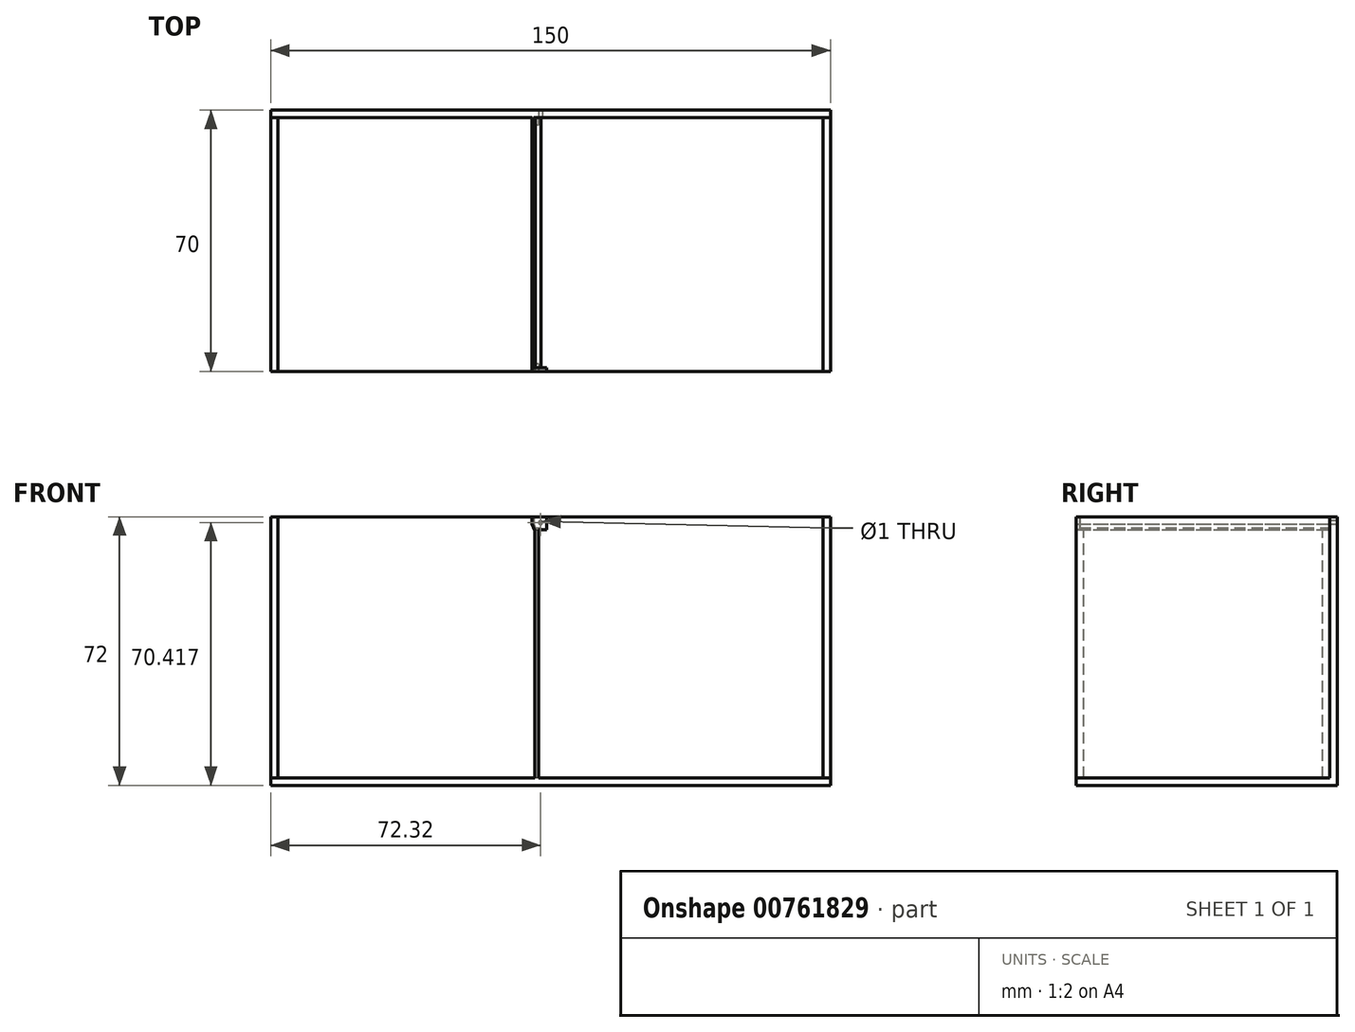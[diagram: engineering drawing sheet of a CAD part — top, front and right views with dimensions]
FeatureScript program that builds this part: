
annotation { "Feature Type Name" : "Feature", "Feature Type Description" : "" }
export const myFeature = defineFeature(function(context is Context, id is Id, definition is map)
    precondition{}
    {
        {
            var Q0;
            Q0=qCreatedBy(makeId("Front.planeOp"),FACE);
            var sketch = newSketch(context, id + "F0", { "sketchPlane" : qUnion([Q0])});
            skLineSegment(sketch, "E0.bottom", {"start": v(75, 35) * mm, "end": v(-75, 35) * mm});
            skLineSegment(sketch, "E0.top", {"start": v(75, -35) * mm, "end": v(-75, -35) * mm});
            skLineSegment(sketch, "E0.left", {"start": v(75, 35) * mm, "end": v(75, -35) * mm});
            skLineSegment(sketch, "E0.right", {"start": v(-75, 35) * mm, "end": v(-75, -35) * mm});
            skPoint(sketch, "E0.middle", {"position": v(0, 0) * mm});
            skSolve(sketch);
        }
        {
            var Q0;
            Q0 = qSketchRegion(id + "F0", true);
            extrude(context, id + "F1", {"entities" : qUnion([Q0]), "depth" : 2 * mm, "offsetDistance" : 25.4 * mm});
        }
        {
            var Q0;
            Q0=makeQuery(id+"F1.opExtrude","SWEPT_FACE",FACE,{"disambiguationData":[OSD([sQuery(id+"F0.wireOp",EDGE,"E0.right")])]});
            var sketch = newSketch(context, id + "F2", { "sketchPlane" : qUnion([Q0])});
            skLineSegment(sketch, "E1.bottom", {"start": v(0, 35) * mm, "end": v(70, 35) * mm});
            skLineSegment(sketch, "E1.top", {"start": v(0, -35) * mm, "end": v(70, -35) * mm});
            skLineSegment(sketch, "E1.left", {"start": v(0, 35) * mm, "end": v(0, -35) * mm});
            skLineSegment(sketch, "E1.right", {"start": v(70, 35) * mm, "end": v(70, -35) * mm});
            skSolve(sketch);
        }
        {
            var Q0;
            {var subQ2=sQuery(id+"F2.wireOp",EDGE,"E1.right");Q0=makeQuery(id+"F2.imprint","IMPRINT",FACE,{"disambiguationData":[TD([[makeQuery(id+"F2.imprint","IMPRINT",EDGE,{"derivedFrom":subQ2}),-1.0]])]});}
            extrude(context, id + "F3", {"entities" : qUnion([Q0]), "oppositeDirection" : true, "depth" : 2 * mm, "offsetDistance" : 25.4 * mm});
        }
        {
            var Q0;
            Q0=makeQuery(id+"F1.opExtrude","SWEPT_FACE",FACE,{"disambiguationData":[OSD([sQuery(id+"F0.wireOp",EDGE,"E0.left")])]});
            var sketch = newSketch(context, id + "F4", { "sketchPlane" : qUnion([Q0])});
            skLineSegment(sketch, "E2.bottom", {"start": v(0, 35) * mm, "end": v(-70, 35) * mm});
            skLineSegment(sketch, "E2.top", {"start": v(0, -35) * mm, "end": v(-70, -35) * mm});
            skLineSegment(sketch, "E2.left", {"start": v(0, 35) * mm, "end": v(0, -35) * mm});
            skLineSegment(sketch, "E2.right", {"start": v(-70, 35) * mm, "end": v(-70, -35) * mm});
            skSolve(sketch);
        }
        {
            var Q0;
            {var subQ2=sQuery(id+"F4.wireOp",EDGE,"E2.right");Q0=makeQuery(id+"F4.imprint","IMPRINT",FACE,{"disambiguationData":[TD([[makeQuery(id+"F4.imprint","IMPRINT",EDGE,{"derivedFrom":subQ2}),1.0]])]});}
            extrude(context, id + "F5", {"entities" : qUnion([Q0]), "oppositeDirection" : true, "depth" : 2 * mm, "offsetDistance" : 25.4 * mm});
        }
        {
            var Q0;
            Q0=makeQuery(id+"F3.opExtrude","SWEPT_FACE",FACE,{"disambiguationData":[OSD([sQuery(id+"F2.wireOp",EDGE,"E1.top")])]});
            var sketch = newSketch(context, id + "F6", { "sketchPlane" : qUnion([Q0])});
            skLineSegment(sketch, "E3.bottom", {"start": v(-75, 70) * mm, "end": v(75, 70) * mm});
            skLineSegment(sketch, "E3.top", {"start": v(-75, 0) * mm, "end": v(75, 0) * mm});
            skLineSegment(sketch, "E3.left", {"start": v(-75, 70) * mm, "end": v(-75, 0) * mm});
            skLineSegment(sketch, "E3.right", {"start": v(75, 70) * mm, "end": v(75, 0) * mm});
            skSolve(sketch);
        }
        {
            var Q0;
            Q0 = qSketchRegion(id + "F6", true);
            extrude(context, id + "F7", {"entities" : qUnion([Q0]), "depth" : 2 * mm, "offsetDistance" : 25.4 * mm});
        }
        {
            var Q0;
            Q0=makeQuery(id+"F1.opExtrude","CAP_FACE",FACE,{"disambiguationData":[OSD([sQuery(id+"F0.wireOp",EDGE,"E0.bottom"),sQuery(id+"F0.wireOp",EDGE,"E0.top"),sQuery(id+"F0.wireOp",EDGE,"E0.left"),sQuery(id+"F0.wireOp",EDGE,"E0.right")])],"isStart":false});
            var sketch = newSketch(context, id + "F8", { "sketchPlane" : qUnion([Q0])});
            skLineSegment(sketch, "E4.bottom", {"start": v(1, 35) * mm, "end": v(-1, 35) * mm});
            skLineSegment(sketch, "E4.top", {"start": v(1, -35) * mm, "end": v(-1, -35) * mm});
            skLineSegment(sketch, "E4.left", {"start": v(1, 35) * mm, "end": v(1, -35) * mm});
            skLineSegment(sketch, "E4.right", {"start": v(-1, 35) * mm, "end": v(-1, -35) * mm});
            skPoint(sketch, "E4.middle", {"position": v(0, 0) * mm});
            skSolve(sketch);
        }
        {
            var Q0;
            {var subQ0=sQuery(id+"F8.wireOp",EDGE,"E4.right");Q0=makeQuery(id+"F8.imprint","IMPRINT",FACE,{"disambiguationData":[TD([[makeQuery(id+"F8.imprint","IMPRINT",EDGE,{"derivedFrom":subQ0}),-1.0]])]});}
            var sketch = newSketch(context, id + "F9", { "sketchPlane" : qUnion([Q0])});
            skCircle(sketch, "E5", {"center": v(-2.68, 33.42) * mm, "radius": 0.5 * mm});
            skSolve(sketch);
        }
        {
            var Q0;
            {var subQ0=sQuery(id+"F8.wireOp",EDGE,"E4.left");Q0=makeQuery(id+"F8.imprint","IMPRINT",FACE,{"disambiguationData":[TD([[makeQuery(id+"F8.imprint","IMPRINT",EDGE,{"derivedFrom":subQ0}),1.0]])]});}
            var sketch = newSketch(context, id + "F10", { "sketchPlane" : qUnion([Q0])});
            skLineSegment(sketch, "E6.right", {"start": v(-5, 35) * mm, "end": v(-5, 34.5) * mm});
            skLineSegment(sketch, "E7.bottom", {"start": v(-5, 35) * mm, "end": v(-4.5, 35) * mm});
            skLineSegment(sketch, "E7.left", {"start": v(-5, 35) * mm, "end": v(-5, 33) * mm});
            skLineSegment(sketch, "E7.right", {"start": v(-4.5, 35) * mm, "end": v(-4.5, 33) * mm});
            skLineSegment(sketch, "E8", {"start": v(-5, 33) * mm, "end": v(-4.35, 31.5) * mm});
            skLineSegment(sketch, "E9", {"start": v(-4.5, 33) * mm, "end": v(-4.07, 32) * mm});
            skLineSegment(sketch, "E10", {"start": v(-3.85, 31.5) * mm, "end": v(-4.35, 31.5) * mm});
            skLineSegment(sketch, "E11.bottom", {"start": v(-4.35, 31.5) * mm, "end": v(-2.56, 31.5) * mm});
            skLineSegment(sketch, "E11.top", {"start": v(-4.07, 32) * mm, "end": v(-2.56, 32) * mm});
            skLineSegment(sketch, "E11.right", {"start": v(-2.56, 31.5) * mm, "end": v(-2.56, 32) * mm});
            skSolve(sketch);
        }
        {
            var Q0;
            Q0 = qSketchRegion(id + "F9", true);
            extrude(context, id + "F11", {"entities" : qUnion([Q0]), "operationType" : NewBodyOperationType.REMOVE, "oppositeDirection" : true, "depth" : 25 * mm, "offsetDistance" : 25 * mm});
        }
        {
            var Q0;
            {var subQ0=sQuery(id+"F8.wireOp",EDGE,"E4.right");Q0=makeQuery(id+"F8.imprint","IMPRINT",FACE,{"disambiguationData":[TD([[makeQuery(id+"F8.imprint","IMPRINT",EDGE,{"derivedFrom":subQ0}),-1.0]])]});}
            var sketch = newSketch(context, id + "F12", { "sketchPlane" : qUnion([Q0])});
            skLineSegment(sketch, "E12.bottom", {"start": v(-4.16, -35.1) * mm, "end": v(-3.16, -35.1) * mm});
            skLineSegment(sketch, "E12.top", {"start": v(-4.16, 31.9) * mm, "end": v(-3.16, 31.9) * mm});
            skLineSegment(sketch, "E12.left", {"start": v(-4.16, -35.1) * mm, "end": v(-4.16, 31.9) * mm});
            skLineSegment(sketch, "E12.right", {"start": v(-3.16, -35.1) * mm, "end": v(-3.16, 31.9) * mm});
            skPoint(sketch, "E12.middle", {"position": v(-3.66, -1.6) * mm});
            skSolve(sketch);
        }
        {
            var Q0;
            Q0 = qSketchRegion(id + "F12", true);
            extrude(context, id + "F13", {"entities" : qUnion([Q0]), "operationType" : NewBodyOperationType.ADD, "depth" : 2 * mm, "offsetDistance" : 25 * mm});
        }
        {
            var Q0;
            Q0=makeQuery(id+"F13.opExtrude","SWEPT_FACE",FACE,{"disambiguationData":[OSD([sQuery(id+"F12.wireOp",EDGE,"E12.left")])]});
            var sketch = newSketch(context, id + "F14", { "sketchPlane" : qUnion([Q0])});
            skLineSegment(sketch, "E13.bottom", {"start": v(68, -35) * mm, "end": v(70, -35) * mm});
            skLineSegment(sketch, "E13.top", {"start": v(68, 31.8) * mm, "end": v(70, 31.8) * mm});
            skLineSegment(sketch, "E13.left", {"start": v(68, -35) * mm, "end": v(68, 31.8) * mm});
            skLineSegment(sketch, "E13.right", {"start": v(70, -35) * mm, "end": v(70, 31.8) * mm});
            skSolve(sketch);
        }
        {
            var Q0;
            Q0 = qSketchRegion(id + "F14", true);
            extrude(context, id + "F15", {"entities" : qUnion([Q0]), "operationType" : NewBodyOperationType.ADD, "oppositeDirection" : true, "depth" : 1 * mm, "offsetDistance" : 25 * mm});
        }
        {
            var Q0;
            {var subQ2=sQuery(id+"F10.wireOp",EDGE,"E7.bottom");Q0=makeQuery(id+"F10.imprint","IMPRINT",FACE,{"disambiguationData":[TD([[makeQuery(id+"F10.imprint","IMPRINT",EDGE,{"derivedFrom":subQ2}),-1.0]])]});}
            extrude(context, id + "F16", {"entities" : qUnion([Q0]), "operationType" : NewBodyOperationType.ADD, "depth" : 68 * mm, "offsetDistance" : 25 * mm});
        }
        {
            var Q0;
            Q0=sQuery(id+"F8.wireOp",EDGE,"E4.right");
            extrude(context, id + "F17", {"bodyType" : ToolBodyType.SURFACE, "surfaceEntities" : qUnion([Q0]), "depth" : 68 * mm, "offsetDistance" : 25 * mm});
        }
        {
            var Q0;
            {var subQ0=sQuery(id+"F10.wireOp",EDGE,"E8");var subQ1=sQuery(id+"F10.wireOp",EDGE,"E7.bottom");var subQ4=sQuery(id+"F10.wireOp",EDGE,"E7.left");var subQ5=sQuery(id+"F10.wireOp",EDGE,"E7.right");var subQ6=sQuery(id+"F10.wireOp",EDGE,"E9");var subQ7=sQuery(id+"F10.wireOp",EDGE,"E11.bottom");Q0=makeQuery(id+"F16.boolean.opBoolean","SPLIT",FACE,{"disambiguationData":[TD([makeQuery(id+"F1.opExtrude","SWEPT_FACE",FACE,{"disambiguationData":[OSD([sQuery(id+"F0.wireOp",EDGE,"E0.bottom")])]})])],"derivedFrom":makeQuery(id+"F16.opExtrude","CAP_FACE",FACE,{"disambiguationData":[OSD([subQ1,subQ4,subQ5,subQ0,subQ6,subQ7,sQuery(id+"F10.wireOp",EDGE,"E11.top"),sQuery(id+"F10.wireOp",EDGE,"E11.right")])],"isStart":false})});}
            var sketch = newSketch(context, id + "F18", { "sketchPlane" : qUnion([Q0])});
            skLineSegment(sketch, "E14", {"start": v(-5, 35) * mm, "end": v(-5, 33) * mm});
            skLineSegment(sketch, "E15", {"start": v(-5, 33) * mm, "end": v(-4.35, 31.5) * mm});
            skLineSegment(sketch, "E16", {"start": v(-4.35, 31.5) * mm, "end": v(-1, 31.5) * mm});
            skLineSegment(sketch, "E17", {"start": v(-1, 31.5) * mm, "end": v(-1, 35) * mm});
            skLineSegment(sketch, "E18", {"start": v(-1, 35) * mm, "end": v(-5, 35) * mm});
            skSolve(sketch);
        }
        {
            var Q0;
            Q0 = qSketchRegion(id + "F18", true);
            extrude(context, id + "F19", {"entities" : qUnion([Q0]), "operationType" : NewBodyOperationType.ADD, "oppositeDirection" : true, "depth" : 1 * mm, "offsetDistance" : 25 * mm});
        }
    });
